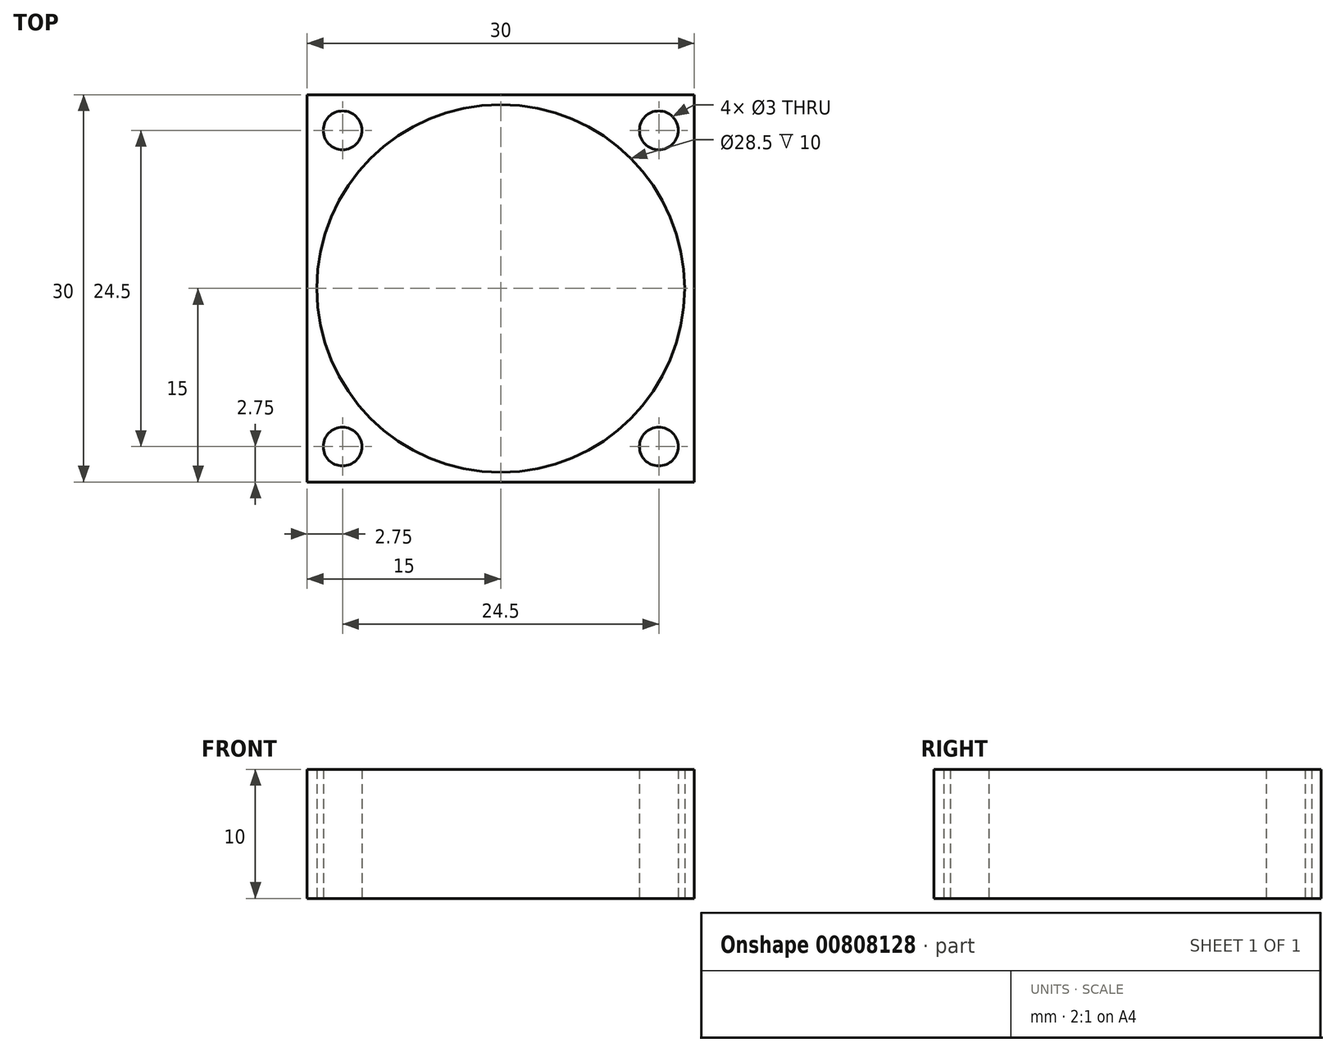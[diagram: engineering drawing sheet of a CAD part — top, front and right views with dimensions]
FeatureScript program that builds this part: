
annotation { "Feature Type Name" : "Feature", "Feature Type Description" : "" }
export const myFeature = defineFeature(function(context is Context, id is Id, definition is map)
    precondition{}
    {
        {
            var Q0;
            Q0=qCreatedBy(makeId("Top.planeOp"),FACE);
            var sketch = newSketch(context, id + "F0", { "sketchPlane" : qUnion([Q0])});
            skLineSegment(sketch, "E0.bottom", {"start": v(15, -15) * mm, "end": v(-15, -15) * mm});
            skLineSegment(sketch, "E0.top", {"start": v(15, 15) * mm, "end": v(-15, 15) * mm});
            skLineSegment(sketch, "E0.left", {"start": v(15, -15) * mm, "end": v(15, 15) * mm});
            skLineSegment(sketch, "E0.right", {"start": v(-15, -15) * mm, "end": v(-15, 15) * mm});
            skPoint(sketch, "E0.middle", {"position": v(0, 0) * mm});
            skCircle(sketch, "E1", {"center": v(-12.25, 12.25) * mm, "radius": 1.5 * mm});
            skCircle(sketch, "E2", {"center": v(12.25, 12.25) * mm, "radius": 1.5 * mm});
            skCircle(sketch, "E3", {"center": v(12.25, -12.25) * mm, "radius": 1.5 * mm});
            skCircle(sketch, "E4", {"center": v(-12.25, -12.25) * mm, "radius": 1.5 * mm});
            skCircle(sketch, "E5", {"center": v(0, 0) * mm, "radius": 14.25 * mm});
            skLineSegment(sketch, "E6", {"start": v(-12.25, -12.25) * mm, "end": v(12.25, 12.25) * mm, "construction": true});
            skSolve(sketch);
        }
        {
            var Q0;
            Q0 = qSketchRegion(id + "F0", true);
            extrude(context, id + "F1", {"entities" : qUnion([Q0]), "depth" : 10 * mm, "offsetDistance" : 25 * mm});
        }
    });
